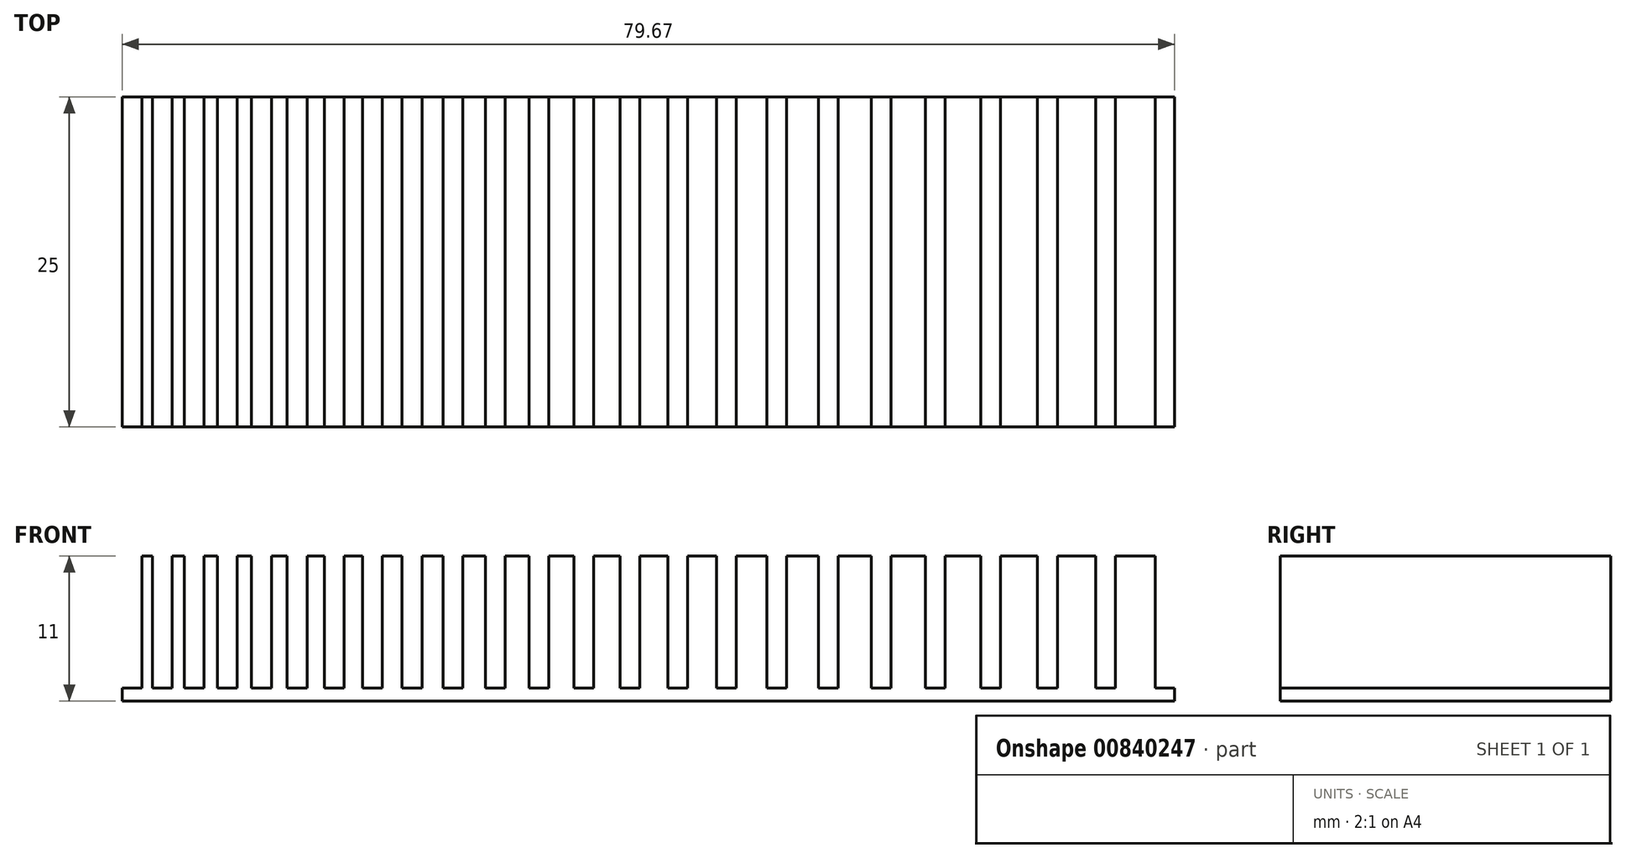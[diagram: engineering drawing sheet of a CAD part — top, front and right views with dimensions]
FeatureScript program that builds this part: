
annotation { "Feature Type Name" : "Feature", "Feature Type Description" : "" }
export const myFeature = defineFeature(function(context is Context, id is Id, definition is map)
    precondition{}
    {
        {
            var Q0;
            Q0=qCreatedBy(makeId("Top.planeOp"),FACE);
            var sketch = newSketch(context, id + "F0", { "sketchPlane" : qUnion([Q0])});
            skLineSegment(sketch, "E0", {"start": v(-48.25, 12.36) * mm, "end": v(-48.25, -12.64) * mm});
            skLineSegment(sketch, "E1", {"start": v(-48.25, -12.64) * mm, "end": v(51.75, -12.64) * mm});
            skLineSegment(sketch, "E2", {"start": v(51.75, -12.64) * mm, "end": v(51.75, 12.36) * mm});
            skLineSegment(sketch, "E3", {"start": v(51.75, 12.36) * mm, "end": v(-48.25, 12.36) * mm});
            skSolve(sketch);
        }
        {
            var Q0;
            Q0=makeQuery(id+"F0.imprint","IMPRINT",FACE,{"disambiguationData":[TD([[makeQuery(id+"F0.imprint","IMPRINT",EDGE,{"derivedFrom":sQuery(id+"F0.wireOp",EDGE,"E0")}),1.0]])]});
            extrude(context, id + "F1", {"entities" : qUnion([Q0]), "depth" : 1 * mm, "offsetDistance" : 25 * mm});
        }
        {
            var Q0;
            Q0=makeQuery(id+"F1.opExtrude","CAP_FACE",FACE,{"disambiguationData":[OSD([sQuery(id+"F0.wireOp",EDGE,"E0"),sQuery(id+"F0.wireOp",EDGE,"E1"),sQuery(id+"F0.wireOp",EDGE,"E2"),sQuery(id+"F0.wireOp",EDGE,"E3")])],"isStart":false});
            var sketch = newSketch(context, id + "F2", { "sketchPlane" : qUnion([Q0])});
            skLineSegment(sketch, "E4", {"start": v(-48.25, 12.36) * mm, "end": v(-46.75, 12.36) * mm, "construction": true});
            skLineSegment(sketch, "E5", {"start": v(-46.75, 12.36) * mm, "end": v(-45.95, 12.36) * mm});
            skLineSegment(sketch, "E6", {"start": v(-45.95, 12.36) * mm, "end": v(-44.45, 12.36) * mm, "construction": true});
            skLineSegment(sketch, "E7", {"start": v(-44.45, 12.36) * mm, "end": v(-43.55, 12.36) * mm});
            skLineSegment(sketch, "E8", {"start": v(-43.55, 12.36) * mm, "end": v(-42.05, 12.36) * mm, "construction": true});
            skLineSegment(sketch, "E9", {"start": v(-42.05, 12.36) * mm, "end": v(-41.05, 12.36) * mm});
            skLineSegment(sketch, "E10", {"start": v(-41.05, 12.36) * mm, "end": v(-39.55, 12.36) * mm, "construction": true});
            skLineSegment(sketch, "E11", {"start": v(-39.55, 12.36) * mm, "end": v(-38.45, 12.36) * mm});
            skLineSegment(sketch, "E12", {"start": v(-38.45, 12.36) * mm, "end": v(-36.95, 12.36) * mm, "construction": true});
            skLineSegment(sketch, "E13", {"start": v(-36.95, 12.36) * mm, "end": v(-35.75, 12.36) * mm});
            skLineSegment(sketch, "E14", {"start": v(-35.75, 12.36) * mm, "end": v(-34.25, 12.36) * mm, "construction": true});
            skLineSegment(sketch, "E15", {"start": v(-34.25, 12.36) * mm, "end": v(-32.95, 12.36) * mm});
            skLineSegment(sketch, "E16", {"start": v(-32.95, 12.36) * mm, "end": v(-31.45, 12.36) * mm, "construction": true});
            skLineSegment(sketch, "E17", {"start": v(-31.45, 12.36) * mm, "end": v(-30.05, 12.36) * mm});
            skLineSegment(sketch, "E18", {"start": v(-30.05, 12.36) * mm, "end": v(-28.55, 12.36) * mm, "construction": true});
            skLineSegment(sketch, "E19", {"start": v(-28.55, 12.36) * mm, "end": v(-27.05, 12.36) * mm});
            skLineSegment(sketch, "E20", {"start": v(-27.05, 12.36) * mm, "end": v(-25.55, 12.36) * mm, "construction": true});
            skLineSegment(sketch, "E21", {"start": v(-25.55, 12.36) * mm, "end": v(-23.95, 12.36) * mm});
            skLineSegment(sketch, "E22", {"start": v(-23.95, 12.36) * mm, "end": v(-22.45, 12.36) * mm, "construction": true});
            skLineSegment(sketch, "E23", {"start": v(-22.45, 12.36) * mm, "end": v(-20.75, 12.36) * mm});
            skLineSegment(sketch, "E24", {"start": v(-20.75, 12.36) * mm, "end": v(-19.25, 12.36) * mm, "construction": true});
            skLineSegment(sketch, "E25", {"start": v(-19.25, 12.36) * mm, "end": v(-17.45, 12.36) * mm});
            skLineSegment(sketch, "E26", {"start": v(-17.45, 12.36) * mm, "end": v(-15.95, 12.36) * mm, "construction": true});
            skLineSegment(sketch, "E27", {"start": v(-15.95, 12.36) * mm, "end": v(-14.05, 12.36) * mm});
            skLineSegment(sketch, "E28", {"start": v(-14.05, 12.36) * mm, "end": v(-12.55, 12.36) * mm, "construction": true});
            skLineSegment(sketch, "E29", {"start": v(-12.55, 12.36) * mm, "end": v(-10.55, 12.36) * mm});
            skLineSegment(sketch, "E30", {"start": v(-10.55, 12.36) * mm, "end": v(-9.05, 12.36) * mm, "construction": true});
            skLineSegment(sketch, "E31", {"start": v(-9.05, 12.36) * mm, "end": v(-6.95, 12.36) * mm});
            skLineSegment(sketch, "E32", {"start": v(-6.95, 12.36) * mm, "end": v(-5.45, 12.36) * mm, "construction": true});
            skLineSegment(sketch, "E33", {"start": v(-5.45, 12.36) * mm, "end": v(-3.25, 12.36) * mm});
            skLineSegment(sketch, "E34", {"start": v(-3.25, 12.36) * mm, "end": v(-1.75, 12.36) * mm, "construction": true});
            skLineSegment(sketch, "E35", {"start": v(-1.75, 12.36) * mm, "end": v(0.55, 12.36) * mm});
            skLineSegment(sketch, "E36", {"start": v(0.55, 12.36) * mm, "end": v(2.05, 12.36) * mm, "construction": true});
            skLineSegment(sketch, "E37", {"start": v(2.05, 12.36) * mm, "end": v(4.45, 12.36) * mm});
            skLineSegment(sketch, "E38", {"start": v(4.45, 12.36) * mm, "end": v(5.95, 12.36) * mm, "construction": true});
            skLineSegment(sketch, "E39", {"start": v(5.95, 12.36) * mm, "end": v(8.45, 12.36) * mm});
            skLineSegment(sketch, "E40", {"start": v(8.45, 12.36) * mm, "end": v(9.95, 12.36) * mm, "construction": true});
            skLineSegment(sketch, "E41", {"start": v(9.95, 12.36) * mm, "end": v(12.55, 12.36) * mm});
            skLineSegment(sketch, "E42", {"start": v(12.55, 12.36) * mm, "end": v(14.05, 12.36) * mm, "construction": true});
            skLineSegment(sketch, "E43", {"start": v(14.05, 12.36) * mm, "end": v(16.75, 12.36) * mm});
            skLineSegment(sketch, "E44", {"start": v(16.75, 12.36) * mm, "end": v(18.25, 12.36) * mm, "construction": true});
            skLineSegment(sketch, "E45", {"start": v(18.25, 12.36) * mm, "end": v(21.05, 12.36) * mm});
            skLineSegment(sketch, "E46", {"start": v(21.05, 12.36) * mm, "end": v(22.55, 12.36) * mm, "construction": true});
            skLineSegment(sketch, "E47", {"start": v(22.55, 12.36) * mm, "end": v(25.45, 12.36) * mm});
            skLineSegment(sketch, "E48", {"start": v(25.45, 12.36) * mm, "end": v(26.95, 12.36) * mm, "construction": true});
            skLineSegment(sketch, "E49", {"start": v(26.95, 12.36) * mm, "end": v(29.95, 12.36) * mm});
            skLineSegment(sketch, "E50", {"start": v(29.95, 12.36) * mm, "end": v(29.95, -12.64) * mm});
            skLineSegment(sketch, "E51", {"start": v(29.95, -12.64) * mm, "end": v(26.95, -12.64) * mm});
            skLineSegment(sketch, "E52", {"start": v(26.95, -12.64) * mm, "end": v(26.95, 12.36) * mm});
            skLineSegment(sketch, "E53", {"start": v(25.45, 12.36) * mm, "end": v(25.45, -12.64) * mm});
            skLineSegment(sketch, "E54", {"start": v(25.45, -12.64) * mm, "end": v(22.55, -12.64) * mm});
            skLineSegment(sketch, "E55", {"start": v(22.55, -12.64) * mm, "end": v(22.55, 12.36) * mm});
            skLineSegment(sketch, "E56", {"start": v(21.05, 12.36) * mm, "end": v(21.05, -12.64) * mm});
            skLineSegment(sketch, "E57", {"start": v(21.05, -12.64) * mm, "end": v(18.25, -12.64) * mm});
            skLineSegment(sketch, "E58", {"start": v(18.25, -12.64) * mm, "end": v(18.25, 12.36) * mm});
            skLineSegment(sketch, "E59", {"start": v(16.75, 12.36) * mm, "end": v(16.75, -12.64) * mm});
            skLineSegment(sketch, "E60", {"start": v(16.75, -12.64) * mm, "end": v(14.05, -12.64) * mm});
            skLineSegment(sketch, "E61", {"start": v(14.05, -12.64) * mm, "end": v(14.05, 12.36) * mm});
            skLineSegment(sketch, "E62", {"start": v(12.55, 12.36) * mm, "end": v(12.55, -12.64) * mm});
            skLineSegment(sketch, "E63", {"start": v(12.55, -12.64) * mm, "end": v(9.95, -12.64) * mm});
            skLineSegment(sketch, "E64", {"start": v(9.95, -12.64) * mm, "end": v(9.95, 12.36) * mm});
            skLineSegment(sketch, "E65", {"start": v(8.45, 12.36) * mm, "end": v(8.45, -12.64) * mm});
            skLineSegment(sketch, "E66", {"start": v(8.45, -12.64) * mm, "end": v(5.95, -12.64) * mm});
            skLineSegment(sketch, "E67", {"start": v(5.95, -12.64) * mm, "end": v(5.95, 12.36) * mm});
            skLineSegment(sketch, "E68", {"start": v(4.45, 12.36) * mm, "end": v(4.45, -12.64) * mm});
            skLineSegment(sketch, "E69", {"start": v(4.45, -12.64) * mm, "end": v(2.05, -12.64) * mm});
            skLineSegment(sketch, "E70", {"start": v(2.05, -12.64) * mm, "end": v(2.05, 12.36) * mm});
            skLineSegment(sketch, "E71", {"start": v(0.55, 12.36) * mm, "end": v(0.55, -12.64) * mm});
            skLineSegment(sketch, "E72", {"start": v(0.55, -12.64) * mm, "end": v(-1.75, -12.64) * mm});
            skLineSegment(sketch, "E73", {"start": v(-1.75, -12.64) * mm, "end": v(-1.75, 12.36) * mm});
            skLineSegment(sketch, "E74", {"start": v(-3.25, 12.36) * mm, "end": v(-3.25, -12.64) * mm});
            skLineSegment(sketch, "E75", {"start": v(-3.25, -12.64) * mm, "end": v(-5.45, -12.64) * mm});
            skLineSegment(sketch, "E76", {"start": v(-5.45, -12.64) * mm, "end": v(-5.45, 12.36) * mm});
            skLineSegment(sketch, "E77", {"start": v(-6.95, 12.36) * mm, "end": v(-6.95, -12.64) * mm});
            skLineSegment(sketch, "E78", {"start": v(-6.95, -12.64) * mm, "end": v(-9.05, -12.64) * mm});
            skLineSegment(sketch, "E79", {"start": v(-9.05, -12.64) * mm, "end": v(-9.05, 12.36) * mm});
            skLineSegment(sketch, "E80", {"start": v(-10.55, 12.36) * mm, "end": v(-10.55, -12.64) * mm});
            skLineSegment(sketch, "E81", {"start": v(-10.55, -12.64) * mm, "end": v(-12.55, -12.64) * mm});
            skLineSegment(sketch, "E82", {"start": v(-12.55, -12.64) * mm, "end": v(-12.55, 12.36) * mm});
            skLineSegment(sketch, "E83", {"start": v(-14.05, 12.36) * mm, "end": v(-14.05, -12.64) * mm});
            skLineSegment(sketch, "E84", {"start": v(-14.05, -12.64) * mm, "end": v(-15.95, -12.64) * mm});
            skLineSegment(sketch, "E85", {"start": v(-15.95, -12.64) * mm, "end": v(-15.95, 12.36) * mm});
            skLineSegment(sketch, "E86", {"start": v(-17.45, 12.36) * mm, "end": v(-17.45, -12.64) * mm});
            skLineSegment(sketch, "E87", {"start": v(-17.45, -12.64) * mm, "end": v(-19.25, -12.64) * mm});
            skLineSegment(sketch, "E88", {"start": v(-19.25, -12.64) * mm, "end": v(-19.25, 12.36) * mm});
            skLineSegment(sketch, "E89", {"start": v(-20.75, 12.36) * mm, "end": v(-20.75, -12.64) * mm});
            skLineSegment(sketch, "E90", {"start": v(-20.75, -12.64) * mm, "end": v(-22.45, -12.64) * mm});
            skLineSegment(sketch, "E91", {"start": v(-22.45, -12.64) * mm, "end": v(-22.45, 12.36) * mm});
            skLineSegment(sketch, "E92", {"start": v(-23.95, 12.36) * mm, "end": v(-23.95, -12.64) * mm});
            skLineSegment(sketch, "E93", {"start": v(-23.95, -12.64) * mm, "end": v(-25.55, -12.64) * mm});
            skLineSegment(sketch, "E94", {"start": v(-25.55, -12.64) * mm, "end": v(-25.55, 12.36) * mm});
            skLineSegment(sketch, "E95", {"start": v(-27.05, 12.36) * mm, "end": v(-27.05, -12.64) * mm});
            skLineSegment(sketch, "E96", {"start": v(-27.05, -12.64) * mm, "end": v(-28.55, -12.64) * mm});
            skLineSegment(sketch, "E97", {"start": v(-28.55, -12.64) * mm, "end": v(-28.55, 12.36) * mm});
            skLineSegment(sketch, "E98", {"start": v(-30.05, 12.36) * mm, "end": v(-30.05, -12.64) * mm});
            skLineSegment(sketch, "E99", {"start": v(-30.05, -12.64) * mm, "end": v(-31.45, -12.64) * mm});
            skLineSegment(sketch, "E100", {"start": v(-31.45, -12.64) * mm, "end": v(-31.45, 12.36) * mm});
            skLineSegment(sketch, "E101", {"start": v(-32.95, 12.36) * mm, "end": v(-32.95, -12.64) * mm});
            skLineSegment(sketch, "E102", {"start": v(-32.95, -12.64) * mm, "end": v(-34.25, -12.64) * mm});
            skLineSegment(sketch, "E103", {"start": v(-34.25, -12.64) * mm, "end": v(-34.25, 12.36) * mm});
            skLineSegment(sketch, "E104", {"start": v(-35.75, 12.36) * mm, "end": v(-35.75, -12.64) * mm});
            skLineSegment(sketch, "E105", {"start": v(-35.75, -12.64) * mm, "end": v(-36.95, -12.64) * mm});
            skLineSegment(sketch, "E106", {"start": v(-36.95, -12.64) * mm, "end": v(-36.95, 12.36) * mm});
            skLineSegment(sketch, "E107", {"start": v(-38.45, 12.36) * mm, "end": v(-38.45, -12.64) * mm});
            skLineSegment(sketch, "E108", {"start": v(-38.45, -12.64) * mm, "end": v(-39.55, -12.64) * mm});
            skLineSegment(sketch, "E109", {"start": v(-39.55, -12.64) * mm, "end": v(-39.55, 12.36) * mm});
            skLineSegment(sketch, "E110", {"start": v(-41.05, 12.36) * mm, "end": v(-41.05, -12.64) * mm});
            skLineSegment(sketch, "E111", {"start": v(-41.05, -12.64) * mm, "end": v(-42.05, -12.64) * mm});
            skLineSegment(sketch, "E112", {"start": v(-42.05, -12.64) * mm, "end": v(-42.05, 12.36) * mm});
            skLineSegment(sketch, "E113", {"start": v(-43.55, 12.36) * mm, "end": v(-43.55, -12.64) * mm});
            skLineSegment(sketch, "E114", {"start": v(-43.55, -12.64) * mm, "end": v(-44.45, -12.64) * mm});
            skLineSegment(sketch, "E115", {"start": v(-44.45, -12.64) * mm, "end": v(-44.45, 12.36) * mm});
            skLineSegment(sketch, "E116", {"start": v(-45.95, 12.36) * mm, "end": v(-45.95, -12.64) * mm});
            skLineSegment(sketch, "E117", {"start": v(-45.95, -12.64) * mm, "end": v(-46.75, -12.64) * mm});
            skLineSegment(sketch, "E118", {"start": v(-46.75, -12.64) * mm, "end": v(-46.75, 12.36) * mm});
            skLineSegment(sketch, "E119", {"start": v(29.95, 12.36) * mm, "end": v(31.45, 12.36) * mm, "construction": true});
            skLineSegment(sketch, "E120", {"start": v(31.45, 12.36) * mm, "end": v(31.45, -12.64) * mm, "construction": true});
            skSolve(sketch);
        }
        {
            var Q0;
            Q0 = qSketchRegion(id + "F2", true);
            extrude(context, id + "F3", {"entities" : qUnion([Q0]), "operationType" : NewBodyOperationType.ADD, "depth" : 10 * mm, "offsetDistance" : 25 * mm});
        }
        {
            var Q0;
            {var subQ0=sQuery(id+"F2.wireOp",EDGE,"E50");Q0=makeQuery(id+"F2.imprint","IMPRINT",FACE,{"disambiguationData":[TD([[makeQuery(id+"F2.imprint","IMPRINT",EDGE,{"derivedFrom":subQ0}),1.0]])]});}
            var sketch = newSketch(context, id + "F4", { "sketchPlane" : qUnion([Q0])});
            skLineSegment(sketch, "E121", {"start": v(31.42, 13.71) * mm, "end": v(31.42, -13.99) * mm});
            skLineSegment(sketch, "E122", {"start": v(31.42, -13.99) * mm, "end": v(54.59, -13.99) * mm});
            skLineSegment(sketch, "E123", {"start": v(54.59, -13.99) * mm, "end": v(54.59, 13.71) * mm});
            skLineSegment(sketch, "E124", {"start": v(54.59, 13.71) * mm, "end": v(31.42, 13.71) * mm});
            skSolve(sketch);
        }
        {
            var Q0;
            Q0 = qSketchRegion(id + "F4", true);
            extrude(context, id + "F5", {"entities" : qUnion([Q0]), "operationType" : NewBodyOperationType.REMOVE, "oppositeDirection" : true, "depth" : 25 * mm, "offsetDistance" : 25 * mm});
        }
    });
